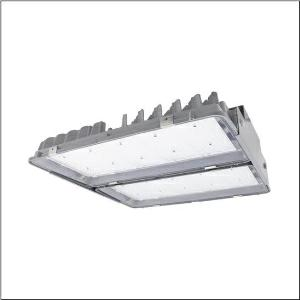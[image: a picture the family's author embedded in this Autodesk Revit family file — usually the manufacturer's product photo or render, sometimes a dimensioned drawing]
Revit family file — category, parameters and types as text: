
# Revit family: highbay_11xtreme_51hf62db4qma
name_source: partatom
category: Lighting Fixtures
units: mm (PartAtom-declared; Revit-internal decimal feet)

## family parameters
Cut with Voids When Loaded = No
Host = Face
Light Source = No
Part Type = Normal
Room Calculation Point = No
Round Connector Dimension = Use Diameter
Shared = No

## types (1)
- --- (1 x LED, 36800 lm, 193.7 W, 4000K)
    Apparent Load = 194 VA
    CIE Flux Codes = 84 96 100 100 100
    Color Rendering = 80
    Color Temperature = 4000K
    Default Elevation = 1800 mm
    Description = Highbay 11Xtreme, LED high bay luminaire, primary light control with lens, of PMMA, primary optical cover: cover, of toughened safety glass, light emission: direct distribution, primary light characteristic: symmetric, installation type: suspended mounting, surface-mounted, 2x LED module,for 1x 2x LED, rated luminous flux: 36.000lm, luminous efficacy: 178lm/W, light colour: 840, colour temperature: 4000K, with cable H07RN-F 5x 1.5mm², mains connection: 220..240V, AC, 50/60Hz, cable length: 1,5m, rated input power: 202W, luminaire housing, of diecast aluminium, coated, silver, length: 595mm, width: 560mm, height: 195mm, protection rating (complete): IP66, insulation class (complete): insulation class I (protective earthing), certification: CE, ENEC, UKCA, protection symbol: D, ball protection: ball impact resistant according to DIN VDE 0710 part 13 (with chain suspension), impact resistance: IK08, permissible operating ambient temperature: -25..+70°C, reducing of maximum allowable ambient temperature of 5°C with ceiling mounting, packaging unit: 1 piece
    Height = 157 mm
    Lamp = 1 x LED
    Lamp Light Flux = 36800 lm
    Lamp Power = 193.7 W
    Lamp count = 1
    Length = 593 mm
    Luminous efficacy = 190 lm/W
    Manufacturer = Siteco
    ModVariant = No
    Model = 51HF62DB4QMA
    Mounting Place = Ceiling
    Mounting Type = Pendant
    Number of Poles = 1
    OnlyDefault = Yes
    Power Factor = 1
    Product Name = Highbay 11Xtreme
    Product group = LED high bay luminaire
    ProductGroupID = 903
    Protection Class = Protection class I
    Protection Degree = IP 66
    RLX_Detail_Level = 1
    RLX_Emergency_Light_Flux = 0 lm
    RLX_Emergency_Type = 0
    RLX_Emergency_Type_DB = No
    RlxData = <blob elided: 34297 chars, md5=59981853>
    Socket = socket
    Standby Power = 0 W
    System Light Flux = 36799 lm
    System Power = 194 W
    Type Comments = factory setting: luminous flux: 100 % | dim-lin: 254 | 648 mA
    Type Image = l_1258340.jpg
    URL = http://relux.com
    VarID = @adj_052641
    Voltage = 0 V
    Weight = 0.00 kg
    Width = 568 mm

## geometry (parser evidence)
native form markers: Blend x4, Sweep x12
no freeform markers — native parametric forms only
